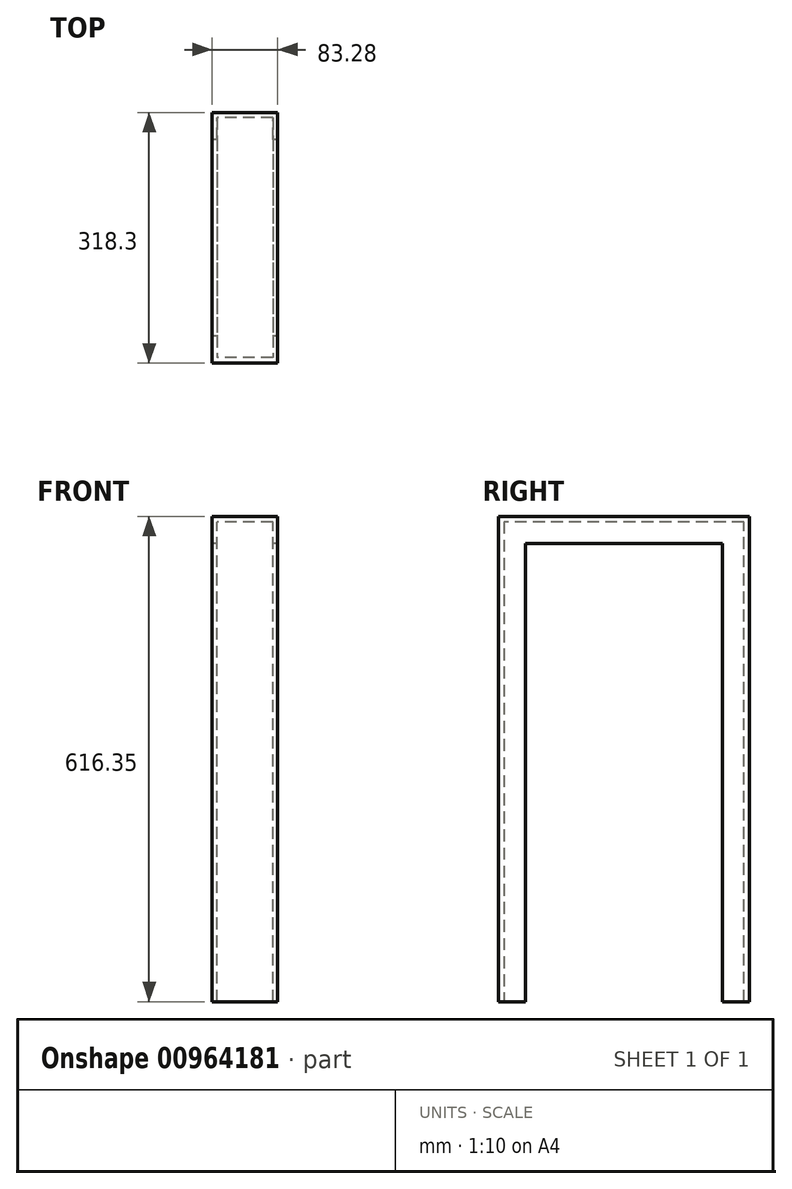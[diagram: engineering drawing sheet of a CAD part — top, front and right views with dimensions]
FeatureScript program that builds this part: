
annotation { "Feature Type Name" : "Feature", "Feature Type Description" : "" }
export const myFeature = defineFeature(function(context is Context, id is Id, definition is map)
    precondition{}
    {
        {
            var Q0;
            Q0=qCreatedBy(makeId("Top.planeOp"),FACE);
            var sketch = newSketch(context, id + "F0", { "sketchPlane" : qUnion([Q0])});
            skLineSegment(sketch, "E0", {"start": v(0, 6.75) * mm, "end": v(-41.64, 6.75) * mm});
            skLineSegment(sketch, "E1", {"start": v(-41.64, 6.75) * mm, "end": v(-41.64, -27.58) * mm});
            skLineSegment(sketch, "E2", {"start": v(-41.64, -27.58) * mm, "end": v(-35.39, -27.58) * mm});
            skLineSegment(sketch, "E3", {"start": v(-35.39, -27.58) * mm, "end": v(-35.39, 0) * mm});
            skLineSegment(sketch, "E4", {"start": v(-35.39, 0) * mm, "end": v(0, 0) * mm});
            skLineSegment(sketch, "E5.MirrorCS", {"start": v(0, 6.75) * mm, "end": v(41.64, 6.75) * mm});
            skLineSegment(sketch, "E6.MirrorCS", {"start": v(35.39, 0) * mm, "end": v(0, 0) * mm});
            skLineSegment(sketch, "E7.MirrorCS", {"start": v(35.39, -27.58) * mm, "end": v(35.39, 0) * mm});
            skLineSegment(sketch, "E8.MirrorCS", {"start": v(41.64, 6.75) * mm, "end": v(41.64, -27.58) * mm});
            skLineSegment(sketch, "E9.MirrorCS", {"start": v(41.64, -27.58) * mm, "end": v(35.39, -27.58) * mm});
            skSolve(sketch);
        }
        {
            var Q0;
            Q0=qCreatedBy(makeId("Right.planeOp"),FACE);
            var sketch = newSketch(context, id + "F1", { "sketchPlane" : qUnion([Q0])});
            skLineSegment(sketch, "E10", {"start": v(0, 0) * mm, "end": v(0, 609.6) * mm});
            skLineSegment(sketch, "E11", {"start": v(0, 609.6) * mm, "end": v(-304.8, 609.6) * mm});
            skLineSegment(sketch, "E12", {"start": v(-304.8, 609.6) * mm, "end": v(-304.8, 0) * mm});
            skSolve(sketch);
        }
        {
            var Q0;
            Q0=makeQuery(id+"F0.imprint","IMPRINT",FACE,{"disambiguationData":[TD([[makeQuery(id+"F0.imprint","IMPRINT",EDGE,{"derivedFrom":sQuery(id+"F0.wireOp",EDGE,"E0")}),1.0]])]});
            var Q1;
            Q1=sQuery(id+"F1.wireOp",EDGE,"E10");
            var Q2;
            Q2=sQuery(id+"F1.wireOp",EDGE,"E11");
            var Q3;
            Q3=sQuery(id+"F1.wireOp",EDGE,"E12");
            sweep(context, id + "F2", {"profiles" : qUnion([Q0]), "path" : qUnion([Q1, Q2, Q3])});
        }
    });
